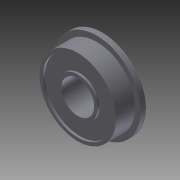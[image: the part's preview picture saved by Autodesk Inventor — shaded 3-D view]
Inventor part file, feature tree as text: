
AUTODESK INVENTOR PART (.ipt)
format: ipt  version: 2012 (Build 160160000, 160)  size: 115,712 bytes
history: native  units: in
note: dims shown in document units (in); Inventor stores cm internally (conversion verified against a paired STEP export)
features: extrude x4, sketch x2
ambient origin geometry x8: Origin, YZ Plane, XZ Plane, XY Plane, X Axis, Y Axis, Z Axis, Center Point
bodies: Solid1 (feature_tree)
feature tree (6):
  sketch  "Sketch1"  dims[d0=0.375in d1=0.875in]
  extrude  "Extrusion1"  Depth=0.875in
  extrude  "Extrusion2"  Depth=0.28in TaperAngle=0.0deg
  extrude  "Extrusion3"  Depth=0.062in TaperAngle=0.0deg
  extrude  "Extrusion4"  Depth=0.8in
  sketch  "Sketch2"  dims[d2=0.999in d3=0.28in d4=0.0in d5=0.062in d6=0.0in d7=0.8in d8=0.45in d9=0.025in d10=0.0in d11=0.025in d12=0.0in]
